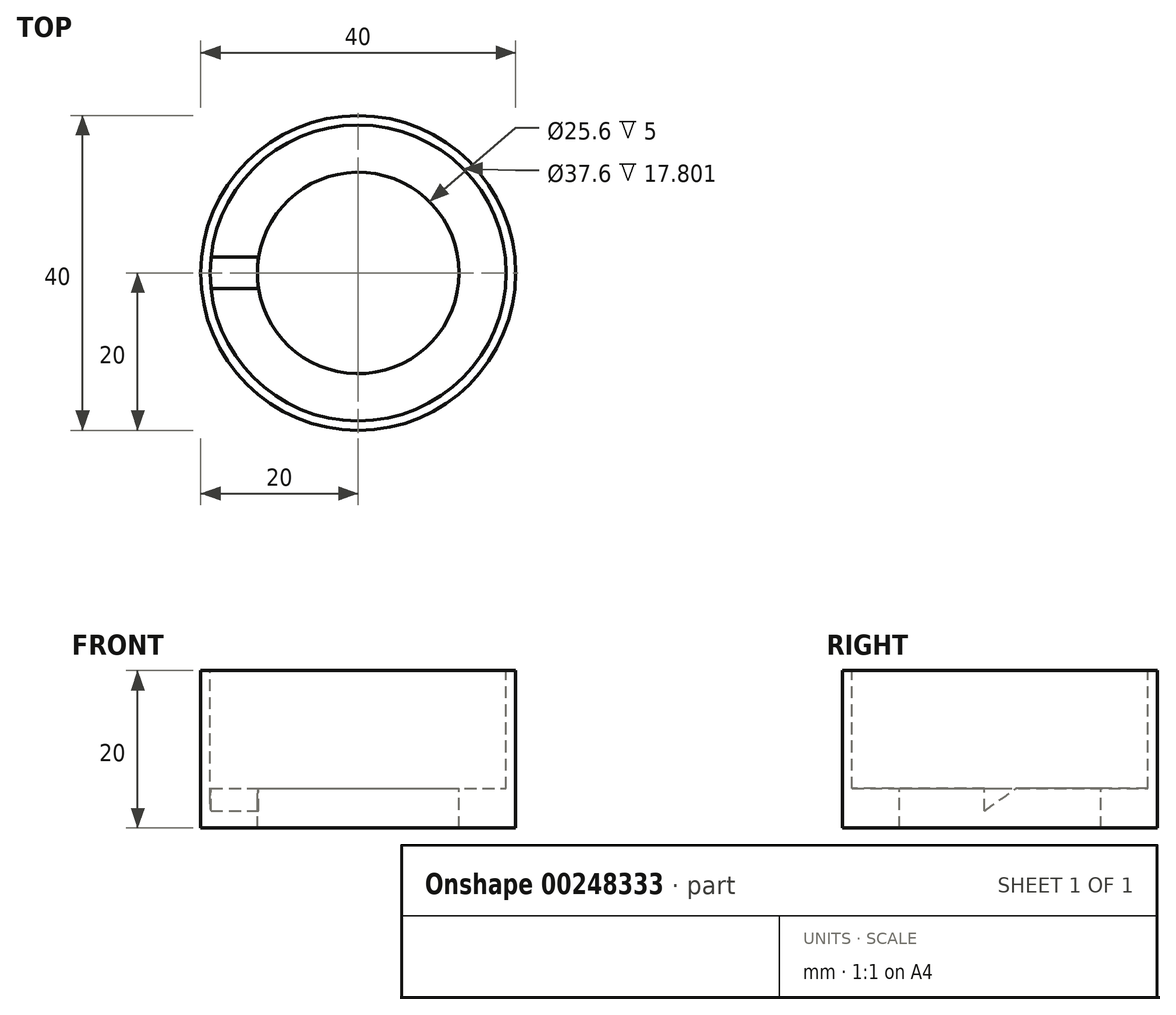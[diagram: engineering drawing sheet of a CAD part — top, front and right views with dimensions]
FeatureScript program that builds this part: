
annotation { "Feature Type Name" : "Feature", "Feature Type Description" : "" }
export const myFeature = defineFeature(function(context is Context, id is Id, definition is map)
    precondition{}
    {
        {
            var Q0;
            Q0=qCreatedBy(makeId("Top.planeOp"),FACE);
            var sketch = newSketch(context, id + "F0", { "sketchPlane" : qUnion([Q0])});
            skCircle(sketch, "E0", {"center": v(0, 0) * mm, "radius": 20 * mm});
            skSolve(sketch);
        }
        {
            var Q0;
            Q0 = qSketchRegion(id + "F0", true);
            extrude(context, id + "F1", {"entities" : qUnion([Q0]), "depth" : 20 * mm});
        }
        {
            var Q0;
            Q0=makeQuery(id+"F1.opExtrude","CAP_FACE",FACE,{"disambiguationData":[OSD([sQuery(id+"F0.wireOp",EDGE,"E0")])],"isStart":false});
            var sketch = newSketch(context, id + "F2", { "sketchPlane" : qUnion([Q0])});
            skCircle(sketch, "E1", {"center": v(0, 0) * mm, "radius": 18.8 * mm});
            skSolve(sketch);
        }
        {
            var Q0;
            Q0 = qSketchRegion(id + "F2", true);
            extrude(context, id + "F3", {"entities" : qUnion([Q0]), "operationType" : NewBodyOperationType.REMOVE, "oppositeDirection" : true, "depth" : 15 * mm});
        }
        {
            var Q0;
            Q0=makeQuery(id+"F3.boolean.opBoolean","COPY",FACE,{"derivedFrom":makeQuery(id+"F3.opExtrude","CAP_FACE",FACE,{"disambiguationData":[OSD([sQuery(id+"F2.wireOp",EDGE,"E1")])],"isStart":false})});
            var sketch = newSketch(context, id + "F4", { "sketchPlane" : qUnion([Q0])});
            skCircle(sketch, "E2", {"center": v(0, 0) * mm, "radius": 12.8 * mm});
            skSolve(sketch);
        }
        {
            var Q0;
            Q0 = qSketchRegion(id + "F4", true);
            extrude(context, id + "F5", {"entities" : qUnion([Q0]), "operationType" : NewBodyOperationType.REMOVE, "oppositeDirection" : true, "depth" : 25 * mm});
        }
        {
            var Q0;
            Q0=qCreatedBy(makeId("Right.planeOp"),FACE);
            var sketch = newSketch(context, id + "F6", { "sketchPlane" : qUnion([Q0])});
            skLineSegment(sketch, "E3", {"start": v(0, 0) * mm, "end": v(0, 3.6) * mm});
            skLineSegment(sketch, "E4", {"start": v(-2, 2.2) * mm, "end": v(0, 3.6) * mm});
            skLineSegment(sketch, "E5", {"start": v(0, 3.6) * mm, "end": v(2, 5) * mm});
            skLineSegment(sketch, "E6", {"start": v(-2, 2.2) * mm, "end": v(-2, 5) * mm});
            skLineSegment(sketch, "E7", {"start": v(-2, 5) * mm, "end": v(2, 5) * mm});
            skSolve(sketch);
        }
        {
            var Q0;
            Q0 = qSketchRegion(id + "F6", true);
            var Q1;
            Q1=makeQuery(id+"F3.boolean.opBoolean","COPY",FACE,{"derivedFrom":makeQuery(id+"F3.opExtrude","SWEPT_FACE",FACE,{"disambiguationData":[OSD([sQuery(id+"F2.wireOp",EDGE,"E1")])]})});
            extrude(context, id + "F7", {"entities" : qUnion([Q0]), "operationType" : NewBodyOperationType.REMOVE, "endBound" : BoundingType.UP_TO_SURFACE, "oppositeDirection" : true, "endBoundEntityFace" : qUnion([Q1]), "depth" : 25 * mm});
        }
    });
